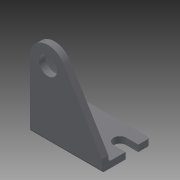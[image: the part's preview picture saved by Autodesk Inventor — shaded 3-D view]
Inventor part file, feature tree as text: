
AUTODESK INVENTOR PART (.ipt)
format: ipt  version: 2014 (Build 180170000, 170)  size: 152,064 bytes
history: native  units: in
note: dims shown in document units (in); Inventor stores cm internally (conversion verified against a paired STEP export)
features: other x14, sketch x8, extrude x5, hole x3
ambient origin geometry x8: Origin, YZ Plane, XZ Plane, XY Plane, X Axis, Y Axis, Z Axis, Center Point
bodies: Solid1 (feature_tree)
feature tree (30):
  extrude  "Extrusion1"  Depth=1.0in TaperAngle=0.0deg
  extrude  "Extrusion2"  Depth=0.1345in TaperAngle=0.0deg
  hole  "Hole1"  [1 undecoded]
  hole  "Hole2"  [1 undecoded]
  hole  "Hole3"  [1 undecoded]
  sketch  "Sketch_6"
  sketch  "Sketch_7"
  extrude  "Extrusion3"  [1 undecoded]
  extrude  "Extrusion4"  [1 undecoded]
  extrude  "Extrusion5"  [1 undecoded]
  other  "to_dummy_R_XY"
  other  "to_dummy_R_YZ"
  other  "to_dummy_R_ZX"
  other  "to_dummy_R_X"
  other  "to_dummy_R_Y"
  other  "to_dummy_R_Z"
  other  "to_dummy_R_Center"
  other  "to_pin_R_XY"
  other  "to_pin_R_YZ"
  other  "to_pin_R_ZX"
  other  "to_pin_R_X"
  other  "to_pin_R_Y"
  other  "to_pin_R_Z"
  other  "to_pin_R_Center"
  sketch  "Sketch_1"  dims[d0=1.5in d1=0.0in d2=1.0in d3=0.0in]
  sketch  "Sketch_2"  dims[d4=0.3775in d5=0.75in d6=0.375in d7=0.25in d8=0.5635in d9=0.1345in d10=0.0in]
  sketch  "Sketch3"  dims[d11=0.266in d12=0.75in d13=0.375in d14=0.25in d15=0.5635in d16=0.1345in d17=0.0in]
  sketch  "Sketch4"  dims[d18=0.266in d19=0.75in d20=0.375in d21=0.25in d22=0.5635in d23=0.1345in d24=0.0in d25=0.1345in d26=0.0in]
  sketch  "Sketch5"  dims[d27=0.1345in d28=0.0in d29=0.1345in d30=0.0in]
  sketch  "Sketch_8"
note: 6 required parameter values undecoded (feature->parameter linkage not recoverable at this tier; creation-order binding heuristic only, values carry confidence <= 0.55)
